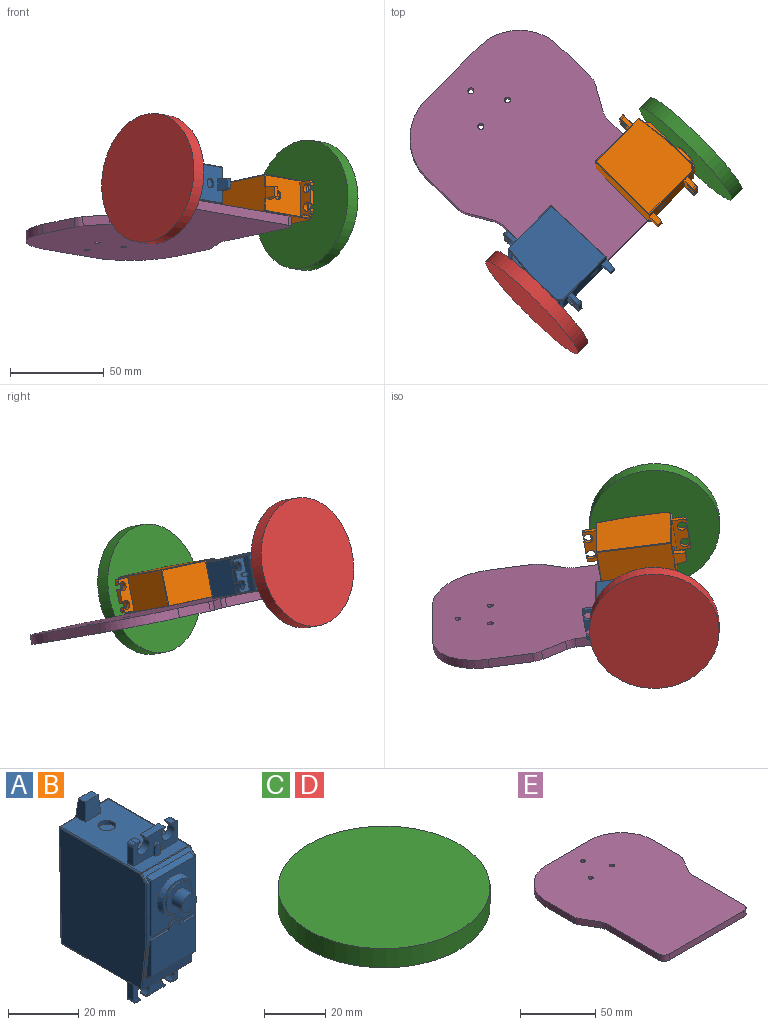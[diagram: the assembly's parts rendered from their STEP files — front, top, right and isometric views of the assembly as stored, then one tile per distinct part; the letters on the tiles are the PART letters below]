
ASSEMBLY  parts=5 mates=2
PART A: 118 faces, bbox 20.1x42.7x55.7 mm
  f0: plane 32.47x19.3mm, normal (0,0,1), area 537.9mm2, adj f39,f44,f54,f55,f56,f58,f59,f60
  f1: plane 10.03x10.03mm, normal (0,-1,0), area 51.1mm2, adj f2,f116
  f2: cylinder r=5.02mm len=10.03mm, axis (0,1,0), area 16mm2, adj f1,f3
  f3: plane 11.67x11.67mm, normal (0,-1,0), area 27.9mm2, adj f2,f4
  f4: cone r=7.18mm half-angle=20deg, axis (0,1,0), area 73.2mm2, adj f3,f16
  f5: plane 2.5x1.68mm, normal (0,0,-1), area 4.2mm2, adj f6,f18,f23,f67
  f6: plane 2.5x0.37mm, normal (-1,0,0), area 0.9mm2, adj f5,f7,f18,f23
  f7: cylinder r=2.5mm len=5mm, axis (0,1,0), area 33.1mm2, adj f6,f8,f18,f23
  f8: plane 2.5x0.37mm, normal (1,0,0), area 0.9mm2, adj f7,f9,f18,f23
  f9: plane 7.64x2.5mm, normal (0,0,-1), area 19.1mm2, adj f8,f10,f18,f23
  f10: plane 2.5x0.37mm, normal (-1,0,0), area 0.9mm2, adj f9,f11,f18,f23
  f11: cylinder r=2.5mm len=5mm, axis (0,1,0), area 33.1mm2, adj f10,f12,f18,f23
  f12: plane 2.5x0.37mm, normal (1,0,0), area 0.9mm2, adj f11,f13,f18,f23
  f13: plane 2.5x1.68mm, normal (0,0,-1), area 4.2mm2, adj f12,f18,f23,f66
  f14: plane 1x0.73mm, normal (0,0,-1), area 0.7mm2, adj f21,f23,f112,f115
  f15: plane 17.91x14.67mm, normal (0,-1,0), area 231.9mm2, adj f27,f28,f29,f30,f31,f32,f106,f107
  f16: plane 19.53x17.91mm, normal (0,-1,0), area 208.2mm2, adj f4,f24,f25,f26,f33,f34,f35,f104
  f17: plane 6.36x2.5mm, normal (-1,0,0), area 15.9mm2, adj f18,f23,f36,f66
  f18: plane 18x7.5mm, normal (0,1,0), area 94.4mm2, adj f5,f6,f7,f8,f9,f10,f11,f12
  f19: plane 6.36x2.5mm, normal (1,0,0), area 15.9mm2, adj f18,f23,f36,f67
  f20: plane 3.37x1mm, normal (1,0,0), area 3.4mm2, adj f21,f23,f36,f112
  f21: plane 4x2mm, normal (0,-1,0), area 7.8mm2, adj f14,f20,f22,f36,f112,f115
  f22: plane 3.37x1mm, normal (-1,0,0), area 3.4mm2, adj f21,f23,f36,f115
  f23: plane 18x7.5mm, normal (0,-1,0), area 86.6mm2, adj f5,f6,f7,f8,f9,f10,f11,f12
  f24: plane 6x0.64mm, normal (0,0,-1), area 3.8mm2, adj f16,f25,f37,f105
  f25: cylinder r=3.37mm len=6.23mm, axis (0,-1,0), area 5.1mm2, adj f16,f24,f26,f37
  f26: plane 4.92x0.64mm, normal (0,0,-1), area 3.1mm2, adj f16,f25,f37,f104
  f27: plane 5.94x0.64mm, normal (0,0,1), area 3.8mm2, adj f15,f28,f37,f107
  f28: cylinder r=2.1mm len=4.19mm, axis (0,-1,0), area 4.2mm2, adj f15,f27,f29,f37
  f29: plane 7.02x0.64mm, normal (0,0,1), area 4.5mm2, adj f15,f28,f37,f106
  f30: plane 17.15x2.21mm, normal (0,-0.71,-0.71), area 53.6mm2, adj f15,f38,f108,f109
  f31: plane 13.8x2.15mm, normal (1,0,0), area 16.9mm2, adj f15,f37,f38,f71,f107,f108
  f32: plane 13.8x2.15mm, normal (-1,0,0), area 16.9mm2, adj f15,f37,f38,f75,f106,f109
  f33: plane 19.17x1.54mm, normal (1,0,0), area 12.3mm2, adj f16,f37,f42,f74,f104,f110
  f34: plane 17.15x2.08mm, normal (0,-0.26,0.97), area 37mm2, adj f16,f42,f110,f111
  f35: plane 19.17x1.54mm, normal (-1,0,0), area 12.3mm2, adj f16,f37,f42,f84,f105,f111
  f36: plane 32.18x19.3mm, normal (0,0,-1), area 574.1mm2, adj f17,f18,f19,f20,f21,f22,f23,f87
  f37: plane 20.14x19.3mm, normal (0,-1,0), area 53.6mm2, adj f24,f25,f26,f27,f28,f29,f31,f32
  f38: plane 19.3x17.42mm, normal (0,-0.99,-0.11), area 79.7mm2, adj f30,f31,f32,f71,f75,f76,f86,f87
  f39: plane 18x7.5mm, normal (0,1,0), area 94.4mm2, adj f0,f44,f45,f46,f47,f48,f49,f50
  f40: plane 40.27x19.3mm, normal (0,1,-0.02), area 772.4mm2, adj f60,f61,f62,f80,f89,f97,f101,f103
  f41: plane 39.88x34.79mm, normal (1,0,0), area 1354.1mm2, adj f73,f76,f82,f83,f88,f89
  f42: plane 19.3x2.32mm, normal (0,-0.71,0.71), area 29.6mm2, adj f33,f34,f35,f74,f83,f84,f94,f95
  f43: plane 39.88x34.79mm, normal (-1,0,0), area 1354.1mm2, adj f85,f86,f95,f96,f100,f101
  f44: plane 6.36x2.5mm, normal (-1,0,0), area 15.9mm2, adj f0,f39,f55,f68
  f45: plane 2.5x1.68mm, normal (0,0,1), area 4.2mm2, adj f39,f46,f55,f68
  f46: plane 2.5x0.37mm, normal (1,0,0), area 0.9mm2, adj f39,f45,f47,f55
  f47: cylinder r=2.5mm len=5mm, axis (0,1,0), area 33.1mm2, adj f39,f46,f48,f55
  f48: plane 2.5x0.37mm, normal (-1,0,0), area 0.9mm2, adj f39,f47,f49,f55
  f49: plane 7.64x2.5mm, normal (0,0,1), area 19.1mm2, adj f39,f48,f50,f55
  f50: plane 2.5x0.37mm, normal (1,0,0), area 0.9mm2, adj f39,f49,f51,f55
  f51: cylinder r=2.5mm len=5mm, axis (0,1,0), area 33.1mm2, adj f39,f50,f52,f55
  f52: plane 2.5x0.37mm, normal (-1,0,0), area 0.9mm2, adj f39,f51,f53,f55
  f53: plane 2.5x1.68mm, normal (0,0,1), area 4.2mm2, adj f39,f52,f55,f65
  f54: plane 6.36x2.5mm, normal (1,0,0), area 15.9mm2, adj f0,f39,f55,f65
  f55: plane 18x7.5mm, normal (0,-1,0), area 86.6mm2, adj f0,f44,f45,f46,f47,f48,f49,f50
  f56: plane 4x2mm, normal (0,-1,0), area 7.8mm2, adj f0,f57,f58,f59,f113,f114
  f57: plane 1x0.73mm, normal (0,0,1), area 0.7mm2, adj f55,f56,f113,f114
  f58: plane 3.37x1mm, normal (1,0,0), area 3.4mm2, adj f0,f55,f56,f114
  f59: plane 3.37x1mm, normal (-1,0,0), area 3.4mm2, adj f0,f55,f56,f113
  f60: plane 6.75x3.82mm, normal (-1,0,0.09), area 20.8mm2, adj f0,f40,f61,f63,f64,f103
  f61: plane 6.35x6.35mm, normal (0,1,0.09), area 36.9mm2, adj f40,f60,f62,f64
  f62: plane 6.75x3.82mm, normal (1,0,0.09), area 20.8mm2, adj f0,f40,f61,f63,f64,f80
  f63: plane 6.35x6.35mm, normal (0,-1,0.09), area 36.9mm2, adj f0,f60,f62,f64
  f64: plane 5.24x2.7mm, normal (0,0,1), area 14.1mm2, adj f60,f61,f62,f63
  f65: cylinder r=1.14mm len=2.5mm, axis (0,1,0), area 4.5mm2, adj f39,f53,f54,f55
  f66: cylinder r=1.14mm len=2.5mm, axis (0,1,0), area 4.5mm2, adj f13,f17,f18,f23
  f67: cylinder r=1.14mm len=2.5mm, axis (0,1,0), area 4.5mm2, adj f5,f18,f19,f23
  f68: cylinder r=1.14mm len=2.5mm, axis (0,1,0), area 4.5mm2, adj f39,f44,f45,f55
  f69: cylinder r=2.54mm len=5.08mm, axis (0,0,1), area 20.3mm2, adj f0,f70
  f70: plane 5.08x5.08mm, normal (0,0,1), area 20.3mm2, adj f69
  f71: cylinder r=0.38mm len=0.7mm, axis (1,0,0), area 0mm2, adj f31,f37,f38,f72
  f72: sphere r=0.38mm, area 0mm2, adj f71,f73,f76
  f73: cylinder r=0.38mm len=20.14mm, axis (0,0,1), area 12.1mm2, adj f37,f41,f72,f77
  f74: cylinder r=0.38mm len=0.7mm, axis (1,0,0), area 0.2mm2, adj f33,f37,f42,f77
  f75: cylinder r=0.38mm len=0.7mm, axis (1,0,0), area 0mm2, adj f32,f37,f38,f78
  f76: cylinder r=0.38mm len=17.46mm, axis (0,-0.11,0.99), area 10.5mm2, adj f38,f41,f72,f79
  f77: sphere r=0.38mm, area 0.1mm2, adj f73,f74,f83
  f78: sphere r=0.38mm, area 0mm2, adj f75,f85,f86
  f79: sphere r=0.38mm, area 0.2mm2, adj f76,f87,f88
  f80: cylinder r=0.38mm len=6.48mm, axis (-1,0,0), area 3.9mm2, adj f0,f40,f62,f81
  f81: sphere r=0.38mm, area 0.2mm2, adj f80,f82,f89
  f82: cylinder r=0.38mm len=32.47mm, axis (0,-1,0), area 19.4mm2, adj f0,f41,f81,f90
  f83: cylinder r=0.38mm len=2.59mm, axis (0,0.71,0.71), area 2mm2, adj f41,f42,f77,f90
  f84: cylinder r=0.38mm len=0.7mm, axis (1,0,0), area 0.2mm2, adj f35,f37,f42,f91
  f85: cylinder r=0.38mm len=20.14mm, axis (0,0,1), area 12.1mm2, adj f37,f43,f78,f91
  f86: cylinder r=0.38mm len=17.46mm, axis (0,-0.11,0.99), area 10.5mm2, adj f38,f43,f78,f92
  f87: cylinder r=0.38mm len=19.3mm, axis (-1,0,0), area 10.7mm2, adj f36,f38,f79,f92
  f88: cylinder r=0.38mm len=32.18mm, axis (0,-1,0), area 19.3mm2, adj f36,f41,f79,f93
  f89: cylinder r=0.38mm len=39.88mm, axis (0,0.02,1), area 23.9mm2, adj f40,f41,f81,f93
  f90: sphere r=0.38mm, area 0.1mm2, adj f82,f83,f94
  f91: sphere r=0.38mm, area 0.1mm2, adj f84,f85,f95
  f92: sphere r=0.38mm, area 0.2mm2, adj f86,f87,f96
  f93: sphere r=0.38mm, area 0.2mm2, adj f88,f89,f97
  f94: cylinder r=0.38mm len=19.3mm, axis (-1,0,0), area 5.8mm2, adj f0,f42,f90,f98
  f95: cylinder r=0.38mm len=2.59mm, axis (0,0.71,0.71), area 2mm2, adj f42,f43,f91,f98
  f96: cylinder r=0.38mm len=32.18mm, axis (0,-1,0), area 19.3mm2, adj f36,f43,f92,f99
  f97: cylinder r=0.38mm len=19.3mm, axis (1,0,0), area 11.4mm2, adj f36,f40,f93,f99
  f98: sphere r=0.38mm, area 0.1mm2, adj f94,f95,f100
  f99: sphere r=0.38mm, area 0.2mm2, adj f96,f97,f101
  f100: cylinder r=0.38mm len=32.47mm, axis (0,-1,0), area 19.4mm2, adj f0,f43,f98,f102
  f101: cylinder r=0.38mm len=39.88mm, axis (0,-0.02,-1), area 23.9mm2, adj f40,f43,f99,f102
  f102: sphere r=0.38mm, area 0.2mm2, adj f100,f101,f103
  f103: cylinder r=0.38mm len=6.48mm, axis (-1,0,0), area 3.9mm2, adj f0,f40,f60,f102
  f104: cylinder r=0.38mm len=0.64mm, axis (0,-1,0), area 0.4mm2, adj f16,f26,f33,f37
  f105: cylinder r=0.38mm len=0.64mm, axis (0,-1,0), area 0.4mm2, adj f16,f24,f35,f37
  f106: cylinder r=0.38mm len=0.64mm, axis (0,-1,0), area 0.4mm2, adj f15,f29,f32,f37
  f107: cylinder r=0.38mm len=0.64mm, axis (0,-1,0), area 0.4mm2, adj f15,f27,f31,f37
  f108: cylinder r=0.38mm len=2.75mm, axis (0,-0.71,0.71), area 1.9mm2, adj f15,f30,f31,f38
  f109: cylinder r=0.38mm len=2.75mm, axis (0,-0.71,0.71), area 1.9mm2, adj f15,f30,f32,f38
  f110: cylinder r=0.38mm len=2.28mm, axis (0,-0.97,-0.26), area 1.2mm2, adj f16,f33,f34,f42
  f111: cylinder r=0.38mm len=2.28mm, axis (0,-0.97,-0.26), area 1.2mm2, adj f16,f34,f35,f42
  f112: cylinder r=0.64mm len=1mm, axis (0,1,0), area 1mm2, adj f14,f20,f21,f23
  f113: cylinder r=0.64mm len=1mm, axis (0,1,0), area 1mm2, adj f55,f56,f57,f59
  f114: cylinder r=0.64mm len=1mm, axis (0,1,0), area 1mm2, adj f55,f56,f57,f58
  f115: cylinder r=0.64mm len=1mm, axis (0,1,0), area 1mm2, adj f14,f21,f22,f23
  f116: cylinder r=2.98mm len=5.97mm, axis (0,1,0), area 78.6mm2, adj f1,f117
  f117: plane 5.97x5.97mm, normal (0,-1,0), area 28mm2, adj f116
PART B: same geometry as A
PART C: 3 faces, bbox 69x69x7.6 mm
  f0: cylinder r=34.5mm len=69mm, axis (0,0,-1), area 1651.8mm2, adj f1,f2
  f1: plane 69x69mm, normal (0,0,1), area 3739.3mm2, adj f0
  f2: plane 69x69mm, normal (0,0,-1), area 3739.3mm2, adj f0
PART D: same geometry as C
PART E: 21 faces, bbox 100x130x5 mm
  f0: plane 23.84x5mm, normal (1,0,0), area 119.2mm2, adj f2,f3,f11,f15
  f1: plane 23.84x5mm, normal (-1,0,0), area 119.2mm2, adj f2,f3,f12,f16
  f2: plane 130x100mm, normal (0,0,1), area 11283.8mm2, adj f0,f1,f4,f5,f6,f7,f8,f9
  f3: plane 130x100mm, normal (0,0,-1), area 11283.8mm2, adj f0,f1,f4,f5,f6,f7,f8,f9
  f4: plane 70x5mm, normal (0,-1,0), area 350mm2, adj f2,f3,f19,f20
  f5: plane 40x5mm, normal (0,1,0), area 200mm2, adj f2,f3,f11,f12
  f6: cylinder r=1.6mm len=5mm, axis (0,0,-1), area 50.3mm2, adj f2,f3
  f7: cylinder r=1.6mm len=5mm, axis (0,0,-1), area 50.3mm2, adj f2,f3
  f8: cylinder r=1.6mm len=5mm, axis (0,0,-1), area 50.3mm2, adj f2,f3
  f9: plane 48.35x5mm, normal (1,0,0), area 241.7mm2, adj f2,f3,f17,f19
  f10: plane 48.35x5mm, normal (-1,0,0), area 241.7mm2, adj f2,f3,f18,f20
  f11: cylinder r=30mm len=30mm, axis (0,0,-1), area 235.6mm2, adj f0,f2,f3,f5
  f12: cylinder r=30mm len=30mm, axis (0,0,1), area 235.6mm2, adj f1,f2,f3,f5
  f13: plane 12.9x7.37mm, normal (0.87,-0.5,0), area 74.3mm2, adj f2,f3,f15,f17
  f14: plane 12.9x7.37mm, normal (-0.87,-0.5,0), area 74.3mm2, adj f2,f3,f16,f18
  f15: cylinder r=10mm len=5mm, axis (0,0,-1), area 25.9mm2, adj f0,f2,f3,f13
  f16: cylinder r=10mm len=5mm, axis (0,0,-1), area 25.9mm2, adj f1,f2,f3,f14
  f17: cylinder r=10mm len=5mm, axis (0,0,-1), area 25.9mm2, adj f2,f3,f9,f13
  f18: cylinder r=10mm len=5mm, axis (0,0,-1), area 25.9mm2, adj f2,f3,f10,f14
  f19: cylinder r=5mm len=5mm, axis (0,0,1), area 39.3mm2, adj f2,f3,f4,f9
  f20: cylinder r=5mm len=5mm, axis (0,0,-1), area 39.3mm2, adj f2,f3,f4,f10
PLACE A rot(axis=(0.28,0.85,-0.45),93.8deg) t=(103.09,-70.43,74.12)mm
PLACE B rot(axis=(0.65,-0.22,0.72),141.8deg) t=(179.68,5.88,60.89)mm
PLACE C rot(axis=(-0.68,-0.34,-0.64),156.2deg) t=(188.9,-3.05,62.81)mm
PLACE D rot(axis=(-0.68,-0.34,-0.64),156.2deg) t=(106.96,-84.69,76.97)mm
PLACE E rot(axis=(-0.23,0.07,0.97),46.7deg) t=(111.16,-5.6,46.38)mm
MATE fastened D.f0 <-> A.f116  axis (0.7,0.7,-0.12) through (112.32,-79.36,76.04)mm
MATE fastened C.f0 <-> B.f116  axis (-0.7,-0.7,0.12) through (188.9,-3.05,62.81)mm
